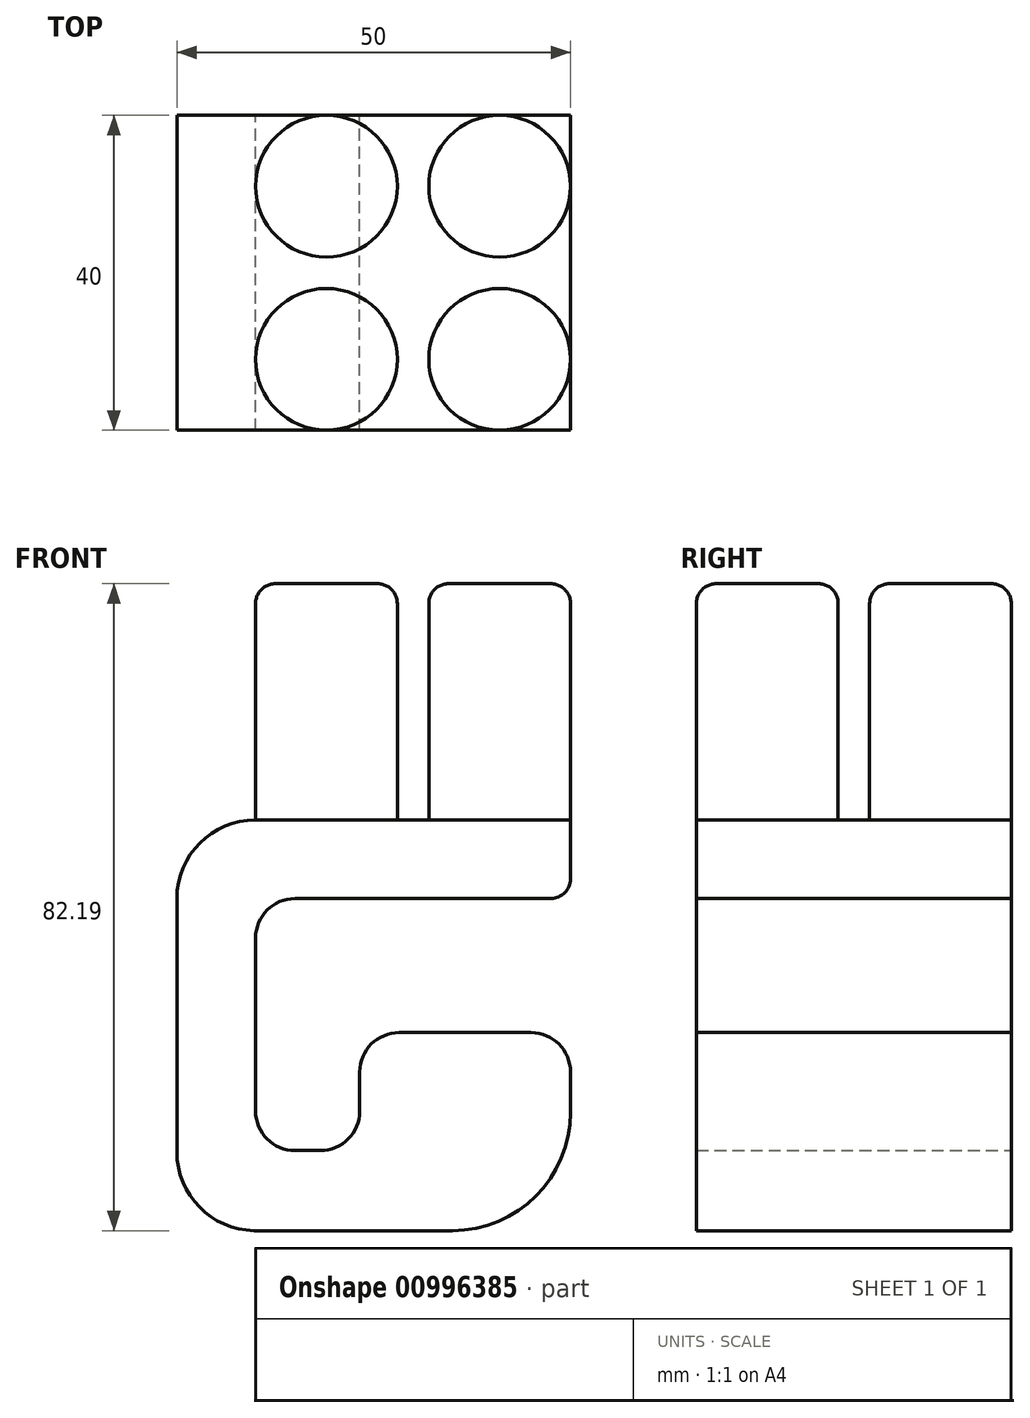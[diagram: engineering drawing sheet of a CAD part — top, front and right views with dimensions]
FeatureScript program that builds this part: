
annotation { "Feature Type Name" : "Feature", "Feature Type Description" : "" }
export const myFeature = defineFeature(function(context is Context, id is Id, definition is map)
    precondition{}
    {
        {
            var Q0;
            Q0=qCreatedBy(makeId("Front.planeOp"),FACE);
            var sketch = newSketch(context, id + "F0", { "sketchPlane" : qUnion([Q0])});
            skLineSegment(sketch, "E0.bottom", {"start": v(17.5, -5) * mm, "end": v(-10, -5) * mm});
            skLineSegment(sketch, "E0.top", {"start": v(20, 5) * mm, "end": v(-20, 5) * mm});
            skLineSegment(sketch, "E0.left", {"start": v(20, -2.5) * mm, "end": v(20, 5) * mm});
            skPoint(sketch, "E0.middle", {"position": v(0, 0) * mm});
            skLineSegment(sketch, "E1.top", {"start": v(-20, 5) * mm, "end": v(-20, 5) * mm});
            skLineSegment(sketch, "E1.right", {"start": v(-30, -5) * mm, "end": v(-30, -5) * mm});
            skPoint(sketch, "E1.middle", {"position": v(-25, 0) * mm});
            skPoint(sketch, "E2.visualSharp", {"position": v(-30, 5) * mm});
            skArc(sketch, "E2.filletArc", {"start": v(-20, 5) * mm, "mid": v(-27.07, 2.07) * mm, "end": v(-30, -5) * mm});
            skLineSegment(sketch, "E3", {"start": v(0, -5) * mm, "end": v(0, -22) * mm, "construction": true});
            skLineSegment(sketch, "E4", {"start": v(-30, -5) * mm, "end": v(-30, -37) * mm});
            skLineSegment(sketch, "E5", {"start": v(-20, -15) * mm, "end": v(-20, -32) * mm});
            skLineSegment(sketch, "E6", {"start": v(-10, -5) * mm, "end": v(-15, -5) * mm});
            skLineSegment(sketch, "E7", {"start": v(-20, -15) * mm, "end": v(-20, -10) * mm});
            skArc(sketch, "E8.filletArc", {"start": v(-15, -5) * mm, "mid": v(-18.54, -6.46) * mm, "end": v(-20, -10) * mm});
            skLineSegment(sketch, "E9.bottom", {"start": v(-48.31, -24.83) * mm, "end": v(-58.31, -24.83) * mm});
            skLineSegment(sketch, "E9.top", {"start": v(-48.31, -14.83) * mm, "end": v(-58.31, -14.83) * mm});
            skLineSegment(sketch, "E9.left", {"start": v(-48.31, -24.83) * mm, "end": v(-48.31, -14.83) * mm});
            skLineSegment(sketch, "E9.right", {"start": v(-58.31, -24.83) * mm, "end": v(-58.31, -14.83) * mm});
            skPoint(sketch, "E9.middle", {"position": v(-53.31, -19.83) * mm});
            skLineSegment(sketch, "E10.bottom", {"start": v(-20, -47.2) * mm, "end": v(-20.18, -47.19) * mm});
            skLineSegment(sketch, "E10.right", {"start": v(-30, -37.2) * mm, "end": v(-30, -37) * mm});
            skPoint(sketch, "E10.middle", {"position": v(-25, -42.1) * mm});
            skLineSegment(sketch, "E11.bottom", {"start": v(-10, -47.2) * mm, "end": v(-20, -47.2) * mm});
            skPoint(sketch, "E12.visualSharp", {"position": v(-30, -47) * mm});
            skArc(sketch, "E12.filletArc", {"start": v(-30, -37.2) * mm, "mid": v(-27.13, -44.2) * mm, "end": v(-20.18, -47.19) * mm});
            skPoint(sketch, "E13.visualSharp", {"position": v(-20, -37) * mm});
            skArc(sketch, "E13.filletArc", {"start": v(-20, -32) * mm, "mid": v(-18.54, -35.54) * mm, "end": v(-15, -37) * mm});
            skLineSegment(sketch, "E14.bottom", {"start": v(-6.83, -47.2) * mm, "end": v(-10, -47.2) * mm});
            skPoint(sketch, "E15.middle", {"position": v(-1.83, -42.1) * mm});
            skPoint(sketch, "E16.middle", {"position": v(-4.81, -36.07) * mm});
            skPoint(sketch, "E17.visualSharp", {"position": v(-6.83, -37) * mm});
            skArc(sketch, "E17.filletArc", {"start": v(-11.77, -37) * mm, "mid": v(-8.24, -35.55) * mm, "end": v(-6.77, -32.03) * mm});
            skLineSegment(sketch, "E18.top", {"start": v(3.17, -22.03) * mm, "end": v(-1.77, -22.03) * mm});
            skLineSegment(sketch, "E18.right", {"start": v(-6.77, -32.03) * mm, "end": v(-6.77, -27.03) * mm});
            skPoint(sketch, "E18.middle", {"position": v(-1.8, -27.03) * mm});
            skPoint(sketch, "E19.visualSharp", {"position": v(-6.77, -22.03) * mm});
            skArc(sketch, "E19.filletArc", {"start": v(-1.77, -22.03) * mm, "mid": v(-5.3, -23.5) * mm, "end": v(-6.77, -27.03) * mm});
            skLineSegment(sketch, "E20", {"start": v(3.17, -22.03) * mm, "end": v(15, -22.03) * mm});
            skPoint(sketch, "E21.visualSharp", {"position": v(-2.8, -35.13) * mm});
            skLineSegment(sketch, "E22", {"start": v(20, -27.03) * mm, "end": v(20, -32.03) * mm});
            skPoint(sketch, "E23.visualSharp", {"position": v(20, -22.03) * mm});
            skArc(sketch, "E23.filletArc", {"start": v(20, -27.03) * mm, "mid": v(18.54, -23.5) * mm, "end": v(15, -22.03) * mm});
            skLineSegment(sketch, "E24", {"start": v(-11.77, -37) * mm, "end": v(-15, -37) * mm});
            skLineSegment(sketch, "E25", {"start": v(20, -5) * mm, "end": v(20, -40.53) * mm, "construction": true});
            skLineSegment(sketch, "E26", {"start": v(-6.83, -47.2) * mm, "end": v(5, -47.2) * mm});
            skLineSegment(sketch, "E27", {"start": v(20, -32.2) * mm, "end": v(20, -32.03) * mm});
            skPoint(sketch, "E28.visualSharp", {"position": v(20, -47.2) * mm});
            skArc(sketch, "E28.filletArc", {"start": v(5, -47.2) * mm, "mid": v(15.6, -42.8) * mm, "end": v(20, -32.2) * mm});
            skPoint(sketch, "E29.visualSharp", {"position": v(20, -5) * mm});
            skArc(sketch, "E29.filletArc", {"start": v(17.5, -5) * mm, "mid": v(19.27, -4.27) * mm, "end": v(20, -2.5) * mm});
            skSolve(sketch);
        }
        {
            var Q0;
            Q0=makeQuery(id+"F0.imprint","IMPRINT",FACE,{"disambiguationData":[TD([[makeQuery(id+"F0.imprint","IMPRINT",EDGE,{"derivedFrom":sQuery(id+"F0.wireOp",EDGE,"E0.bottom")}),-1.0]])]});
            var Q1;
            Q1=makeQuery(id+"F0.imprint","IMPRINT",FACE,{"disambiguationData":[TD([[makeQuery(id+"F0.imprint","IMPRINT",EDGE,{"derivedFrom":sQuery(id+"F0.wireOp",EDGE,"E15.right")}),-1.0]])]});
            var Q2;
            Q2=makeQuery(id+"F0.imprint","IMPRINT",FACE,{"disambiguationData":[TD([[makeQuery(id+"F0.imprint","IMPRINT",EDGE,{"derivedFrom":sQuery(id+"F0.wireOp",EDGE,"E18.bottom")}),-1.0]])]});
            var Q3;
            Q3=makeQuery(id+"F0.imprint","IMPRINT",FACE,{"disambiguationData":[TD([[makeQuery(id+"F0.imprint","IMPRINT",EDGE,{"derivedFrom":sQuery(id+"F0.wireOp",EDGE,"E14.bottom")}),-1.0]])]});
            extrude(context, id + "F1", {"entities" : qUnion([Q0, Q1, Q2, Q3]), "endBound" : BoundingType.SYMMETRIC, "depth" : 40 * mm, "offsetDistance" : 25 * mm});
        }
        {
            var Q0;
            Q0=makeQuery(id+"F1.opExtrude","SWEPT_FACE",FACE,{"disambiguationData":[OSD([sQuery(id+"F0.wireOp",EDGE,"E0.top")])]});
            var sketch = newSketch(context, id + "F2", { "sketchPlane" : qUnion([Q0])});
            skLineSegment(sketch, "E30.left", {"start": v(0, -20) * mm, "end": v(0, 20) * mm});
            skLineSegment(sketch, "E31.top", {"start": v(42.29, 57.77) * mm, "end": v(44.29, 57.77) * mm});
            skPoint(sketch, "E31.middle", {"position": v(43.29, 37.77) * mm});
            skLineSegment(sketch, "E32", {"start": v(0, 20) * mm, "end": v(-2, 20) * mm});
            skLineSegment(sketch, "E33", {"start": v(-2, 20) * mm, "end": v(-2, -20) * mm});
            skLineSegment(sketch, "E34", {"start": v(-2, -20) * mm, "end": v(0, -20) * mm});
            skLineSegment(sketch, "E35", {"start": v(0, 20) * mm, "end": v(2, 20) * mm});
            skLineSegment(sketch, "E36", {"start": v(2, 20) * mm, "end": v(2, -20) * mm});
            skLineSegment(sketch, "E37", {"start": v(2, -20) * mm, "end": v(0, -20) * mm});
            skLineSegment(sketch, "E38", {"start": v(-20, 0) * mm, "end": v(20, 0) * mm});
            skLineSegment(sketch, "E39", {"start": v(20, 0) * mm, "end": v(20, 2) * mm});
            skLineSegment(sketch, "E40", {"start": v(20, 2) * mm, "end": v(-20, 2) * mm});
            skLineSegment(sketch, "E41", {"start": v(-20, 2) * mm, "end": v(-20, 0) * mm});
            skLineSegment(sketch, "E42", {"start": v(-20, 0) * mm, "end": v(-20, -2) * mm});
            skLineSegment(sketch, "E43", {"start": v(-20, -2) * mm, "end": v(20, -2) * mm});
            skLineSegment(sketch, "E44", {"start": v(20, -2) * mm, "end": v(20, 0) * mm});
            skLineSegment(sketch, "E45", {"start": v(11, 20) * mm, "end": v(11, -20) * mm});
            skLineSegment(sketch, "E46", {"start": v(11, 20) * mm, "end": v(20, 20) * mm});
            skLineSegment(sketch, "E47", {"start": v(-11, 20) * mm, "end": v(-11, -20) * mm});
            skLineSegment(sketch, "E48", {"start": v(-11, -20) * mm, "end": v(-20, -20) * mm});
            skLineSegment(sketch, "E49", {"start": v(-20, 11) * mm, "end": v(20, 11) * mm});
            skLineSegment(sketch, "E50", {"start": v(20, 11) * mm, "end": v(20, 20) * mm});
            skLineSegment(sketch, "E51", {"start": v(-20, -11) * mm, "end": v(20, -11) * mm});
            skLineSegment(sketch, "E52", {"start": v(20, -11) * mm, "end": v(20, -20) * mm});
            skCircle(sketch, "E53", {"center": v(11, 11) * mm, "radius": 9 * mm});
            skCircle(sketch, "E54", {"center": v(11, -11) * mm, "radius": 9 * mm});
            skCircle(sketch, "E55", {"center": v(-11, -11) * mm, "radius": 9 * mm});
            skCircle(sketch, "E56", {"center": v(-11, 11) * mm, "radius": 9 * mm});
            skSolve(sketch);
        }
        {
            var Q0;
            {var subQ1=sQuery(id+"F2.wireOp",EDGE,"E47");var subQ3=sQuery(id+"F2.wireOp",EDGE,"E49");var subQ4=makeQuery(id+"F2.imprint","INTERSECT",VERTEX,{"derivedFrom":[subQ1,subQ3]});Q0=makeQuery(id+"F2.imprint","IMPRINT",FACE,{"disambiguationData":[TD([[makeQuery(id+"F2.imprint","IMPRINT",EDGE,{"disambiguationData":[TD([[subQ4,1.0]])],"derivedFrom":subQ1}),1.0]])]});}
            var Q1;
            {var subQ1=sQuery(id+"F2.wireOp",EDGE,"E47");var subQ4=sQuery(id+"F2.wireOp",EDGE,"E49");var subQ5=makeQuery(id+"F2.imprint","INTERSECT",VERTEX,{"derivedFrom":[subQ1,subQ4]});Q1=makeQuery(id+"F2.imprint","IMPRINT",FACE,{"disambiguationData":[TD([[makeQuery(id+"F2.imprint","IMPRINT",EDGE,{"disambiguationData":[TD([[subQ5,1.0]])],"derivedFrom":subQ1}),-1.0]])]});}
            var Q2;
            {var subQ0=sQuery(id+"F2.wireOp",EDGE,"E49");var subQ1=sQuery(id+"F2.wireOp",EDGE,"E47");var subQ2=makeQuery(id+"F2.imprint","INTERSECT",VERTEX,{"derivedFrom":[subQ1,subQ0]});Q2=makeQuery(id+"F2.imprint","IMPRINT",FACE,{"disambiguationData":[TD([[makeQuery(id+"F2.imprint","IMPRINT",EDGE,{"disambiguationData":[TD([[subQ2,-1.0]])],"derivedFrom":subQ1}),-1.0]])]});}
            var Q3;
            {var subQ0=sQuery(id+"F2.wireOp",EDGE,"E49");var subQ1=sQuery(id+"F2.wireOp",EDGE,"E47");var subQ2=makeQuery(id+"F2.imprint","INTERSECT",VERTEX,{"derivedFrom":[subQ1,subQ0]});Q3=makeQuery(id+"F2.imprint","IMPRINT",FACE,{"disambiguationData":[TD([[makeQuery(id+"F2.imprint","IMPRINT",EDGE,{"disambiguationData":[TD([[subQ2,-1.0]])],"derivedFrom":subQ1}),1.0]])]});}
            var Q4;
            {var subQ1=sQuery(id+"F2.wireOp",EDGE,"E45");var subQ3=sQuery(id+"F2.wireOp",EDGE,"E49");var subQ4=makeQuery(id+"F2.imprint","INTERSECT",VERTEX,{"derivedFrom":[subQ1,subQ3]});Q4=makeQuery(id+"F2.imprint","IMPRINT",FACE,{"disambiguationData":[TD([[makeQuery(id+"F2.imprint","IMPRINT",EDGE,{"disambiguationData":[TD([[subQ4,1.0]])],"derivedFrom":subQ3}),1.0]])]});}
            var Q5;
            {var subQ1=sQuery(id+"F2.wireOp",EDGE,"E45");var subQ4=sQuery(id+"F2.wireOp",EDGE,"E49");var subQ5=makeQuery(id+"F2.imprint","INTERSECT",VERTEX,{"derivedFrom":[subQ1,subQ4]});Q5=makeQuery(id+"F2.imprint","IMPRINT",FACE,{"disambiguationData":[TD([[makeQuery(id+"F2.imprint","IMPRINT",EDGE,{"disambiguationData":[TD([[subQ5,1.0]])],"derivedFrom":subQ1}),1.0]])]});}
            var Q6;
            {var subQ0=sQuery(id+"F2.wireOp",EDGE,"E49");var subQ1=sQuery(id+"F2.wireOp",EDGE,"E45");var subQ2=makeQuery(id+"F2.imprint","INTERSECT",VERTEX,{"derivedFrom":[subQ1,subQ0]});Q6=makeQuery(id+"F2.imprint","IMPRINT",FACE,{"disambiguationData":[TD([[makeQuery(id+"F2.imprint","IMPRINT",EDGE,{"disambiguationData":[TD([[subQ2,-1.0]])],"derivedFrom":subQ1}),1.0]])]});}
            var Q7;
            {var subQ0=sQuery(id+"F2.wireOp",EDGE,"E49");var subQ1=sQuery(id+"F2.wireOp",EDGE,"E45");var subQ2=makeQuery(id+"F2.imprint","INTERSECT",VERTEX,{"derivedFrom":[subQ1,subQ0]});Q7=makeQuery(id+"F2.imprint","IMPRINT",FACE,{"disambiguationData":[TD([[makeQuery(id+"F2.imprint","IMPRINT",EDGE,{"disambiguationData":[TD([[subQ2,-1.0]])],"derivedFrom":subQ1}),-1.0]])]});}
            var Q8;
            {var subQ0=sQuery(id+"F2.wireOp",EDGE,"E51");var subQ1=sQuery(id+"F2.wireOp",EDGE,"E45");var subQ2=makeQuery(id+"F2.imprint","INTERSECT",VERTEX,{"derivedFrom":[subQ1,subQ0]});Q8=makeQuery(id+"F2.imprint","IMPRINT",FACE,{"disambiguationData":[TD([[makeQuery(id+"F2.imprint","IMPRINT",EDGE,{"disambiguationData":[TD([[subQ2,1.0]])],"derivedFrom":subQ1}),-1.0]])]});}
            var Q9;
            {var subQ0=sQuery(id+"F2.wireOp",EDGE,"E51");var subQ1=sQuery(id+"F2.wireOp",EDGE,"E45");var subQ2=makeQuery(id+"F2.imprint","INTERSECT",VERTEX,{"derivedFrom":[subQ1,subQ0]});Q9=makeQuery(id+"F2.imprint","IMPRINT",FACE,{"disambiguationData":[TD([[makeQuery(id+"F2.imprint","IMPRINT",EDGE,{"disambiguationData":[TD([[subQ2,1.0]])],"derivedFrom":subQ1}),1.0]])]});}
            var Q10;
            {var subQ1=sQuery(id+"F2.wireOp",EDGE,"E45");var subQ4=sQuery(id+"F2.wireOp",EDGE,"E51");var subQ5=makeQuery(id+"F2.imprint","INTERSECT",VERTEX,{"derivedFrom":[subQ1,subQ4]});Q10=makeQuery(id+"F2.imprint","IMPRINT",FACE,{"disambiguationData":[TD([[makeQuery(id+"F2.imprint","IMPRINT",EDGE,{"disambiguationData":[TD([[subQ5,-1.0]])],"derivedFrom":subQ1}),1.0]])]});}
            var Q11;
            {var subQ1=sQuery(id+"F2.wireOp",EDGE,"E45");var subQ3=sQuery(id+"F2.wireOp",EDGE,"E51");var subQ4=makeQuery(id+"F2.imprint","INTERSECT",VERTEX,{"derivedFrom":[subQ1,subQ3]});Q11=makeQuery(id+"F2.imprint","IMPRINT",FACE,{"disambiguationData":[TD([[makeQuery(id+"F2.imprint","IMPRINT",EDGE,{"disambiguationData":[TD([[subQ4,-1.0]])],"derivedFrom":subQ1}),-1.0]])]});}
            var Q12;
            {var subQ1=sQuery(id+"F2.wireOp",EDGE,"E47");var subQ3=sQuery(id+"F2.wireOp",EDGE,"E51");var subQ4=makeQuery(id+"F2.imprint","INTERSECT",VERTEX,{"derivedFrom":[subQ1,subQ3]});Q12=makeQuery(id+"F2.imprint","IMPRINT",FACE,{"disambiguationData":[TD([[makeQuery(id+"F2.imprint","IMPRINT",EDGE,{"disambiguationData":[TD([[subQ4,-1.0]])],"derivedFrom":subQ3}),-1.0]])]});}
            var Q13;
            {var subQ1=sQuery(id+"F2.wireOp",EDGE,"E47");var subQ4=sQuery(id+"F2.wireOp",EDGE,"E51");var subQ5=makeQuery(id+"F2.imprint","INTERSECT",VERTEX,{"derivedFrom":[subQ1,subQ4]});Q13=makeQuery(id+"F2.imprint","IMPRINT",FACE,{"disambiguationData":[TD([[makeQuery(id+"F2.imprint","IMPRINT",EDGE,{"disambiguationData":[TD([[subQ5,-1.0]])],"derivedFrom":subQ1}),-1.0]])]});}
            var Q14;
            {var subQ0=sQuery(id+"F2.wireOp",EDGE,"E51");var subQ1=sQuery(id+"F2.wireOp",EDGE,"E47");var subQ2=makeQuery(id+"F2.imprint","INTERSECT",VERTEX,{"derivedFrom":[subQ1,subQ0]});Q14=makeQuery(id+"F2.imprint","IMPRINT",FACE,{"disambiguationData":[TD([[makeQuery(id+"F2.imprint","IMPRINT",EDGE,{"disambiguationData":[TD([[subQ2,1.0]])],"derivedFrom":subQ1}),-1.0]])]});}
            var Q15;
            {var subQ0=sQuery(id+"F2.wireOp",EDGE,"E51");var subQ1=sQuery(id+"F2.wireOp",EDGE,"E47");var subQ2=makeQuery(id+"F2.imprint","INTERSECT",VERTEX,{"derivedFrom":[subQ1,subQ0]});Q15=makeQuery(id+"F2.imprint","IMPRINT",FACE,{"disambiguationData":[TD([[makeQuery(id+"F2.imprint","IMPRINT",EDGE,{"disambiguationData":[TD([[subQ2,1.0]])],"derivedFrom":subQ1}),1.0]])]});}
            extrude(context, id + "F3", {"entities" : qUnion([Q0, Q1, Q2, Q3, Q4, Q5, Q6, Q7, Q8, Q9, Q10, Q11, Q12, Q13, Q14, Q15]), "operationType" : NewBodyOperationType.ADD, "depth" : 30 * mm, "offsetDistance" : 25 * mm});
        }
        {
            var Q0;
            Q0=makeQuery(id+"F3.opExtrude","CAP_FACE",FACE,{"disambiguationData":[OSD([sQuery(id+"F2.wireOp",EDGE,"E56")])],"isStart":false});
            var Q1;
            Q1=makeQuery(id+"F3.opExtrude","CAP_FACE",FACE,{"disambiguationData":[OSD([sQuery(id+"F2.wireOp",EDGE,"E53")])],"isStart":false});
            var Q2;
            Q2=makeQuery(id+"F3.opExtrude","CAP_FACE",FACE,{"disambiguationData":[OSD([sQuery(id+"F2.wireOp",EDGE,"E54")])],"isStart":false});
            var Q3;
            Q3=makeQuery(id+"F3.opExtrude","CAP_FACE",FACE,{"disambiguationData":[OSD([sQuery(id+"F2.wireOp",EDGE,"E55")])],"isStart":false});
            fillet(context, id + "F4", {"entities" : qUnion([Q0, Q1, Q2, Q3]), "radius" : 2.5 * mm, "tangentPropagation" : true, "allowEdgeOverflow" : false});
        }
    });
